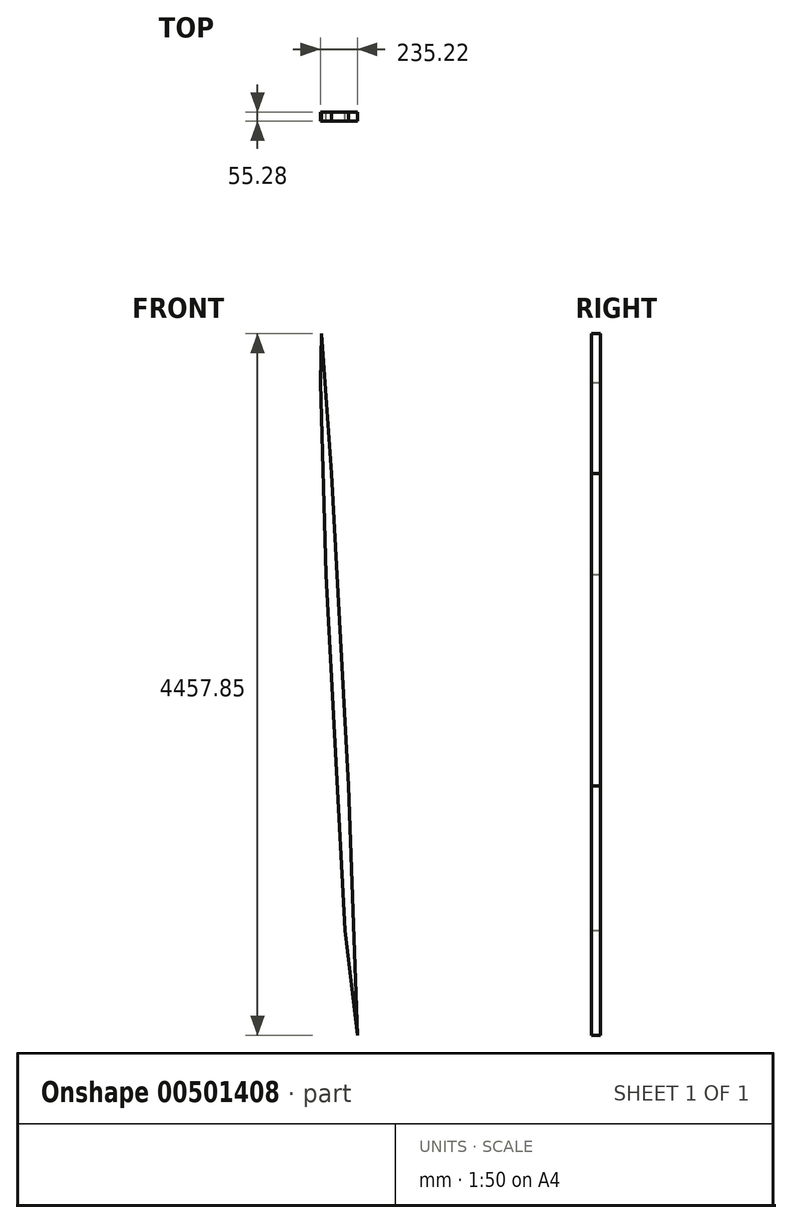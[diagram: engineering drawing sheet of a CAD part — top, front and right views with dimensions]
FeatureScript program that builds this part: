
annotation { "Feature Type Name" : "Feature", "Feature Type Description" : "" }
export const myFeature = defineFeature(function(context is Context, id is Id, definition is map)
    precondition{}
    {
        {
            var Q0;
            Q0=qCreatedBy(makeId("Front.planeOp"),FACE);
            var sketch = newSketch(context, id + "F0", { "sketchPlane" : qUnion([Q0])});
            skLineSegment(sketch, "E0", {"start": v(-52.93, 282.52) * mm, "end": v(-89.4, 1502.23) * mm});
            skLineSegment(sketch, "E1", {"start": v(-89.4, 1502.23) * mm, "end": v(-81.4, 1814.28) * mm});
            skLineSegment(sketch, "E2", {"start": v(-81.4, 1814.28) * mm, "end": v(-20.32, 926.35) * mm});
            skLineSegment(sketch, "E3", {"start": v(-20.32, 926.35) * mm, "end": v(89.27, -1060.73) * mm});
            skLineSegment(sketch, "E4", {"start": v(89.27, -1060.73) * mm, "end": v(145.82, -2643.57) * mm});
            skLineSegment(sketch, "E5", {"start": v(145.82, -2643.57) * mm, "end": v(67.5, -1976.8) * mm});
            skLineSegment(sketch, "E6", {"start": v(67.5, -1976.8) * mm, "end": v(-52.93, 282.52) * mm});
            skSolve(sketch);
        }
        {
            var Q0;
            Q0=makeQuery(id+"F0.imprint","IMPRINT",FACE,{"disambiguationData":[TD([[makeQuery(id+"F0.imprint","IMPRINT",EDGE,{"derivedFrom":sQuery(id+"F0.wireOp",EDGE,"E0")}),-1.0]])]});
            extrude(context, id + "F1", {"entities" : qUnion([Q0]), "depth" : 55.28 * mm});
        }
    });
